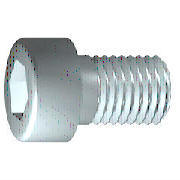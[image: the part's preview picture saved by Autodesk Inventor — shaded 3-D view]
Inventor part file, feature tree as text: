
AUTODESK INVENTOR PART (.ipt)
format: ipt  version: 2016 (Build 200138000, 138)  size: 198,656 bytes
history: native  units: mm (DEFAULTED — no unit token found)
features: sketch x2, extrude x1, plane x1, fillet x1
ambient origin geometry x7: Origin, YZ Plane, XY Plane, X Axis, Y Axis, Z Axis, Center Point
bodies: Solid1 (feature_tree), Body (feature_tree)
feature tree (5):
  extrude  "Slot"  Depth=4.0mm
  plane  "Work Plane1"
  fillet  "Fillet2"  Radius=4.0mm
  sketch  "Sketch1"  dims[d1=10.25mm d2=0.429515mm d3=4.0mm]
  sketch  "Sketch2"  dims[d4=2.0mm d5=60.0deg d6=4.0mm d7=4.0mm d8=3.464102mm d9=7.0mm d10=90.0deg d11=10.0mm d12=0.0mm d13=10.25mm d14=0.0mm d15=0.429415mm d16=0.429415mm d17=0.4mm d19=0.0mm d26=12.0mm d27=45.0deg d28=0.0mm d29=0.0mm d30=0.1mm]
